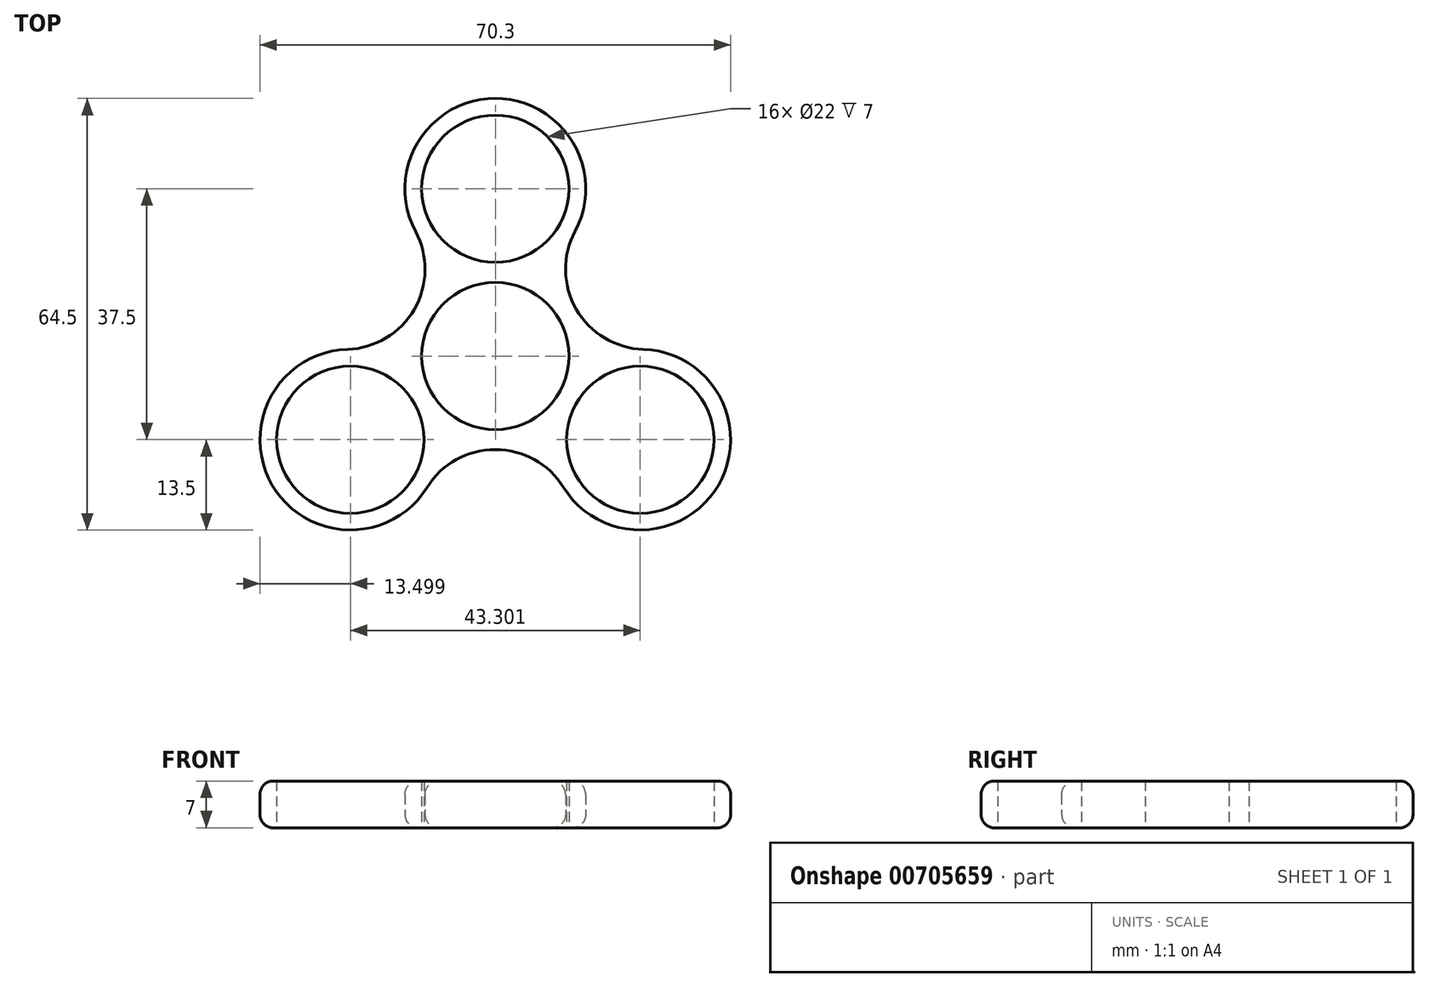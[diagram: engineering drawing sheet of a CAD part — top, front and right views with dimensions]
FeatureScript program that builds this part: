
annotation { "Feature Type Name" : "Feature", "Feature Type Description" : "" }
export const myFeature = defineFeature(function(context is Context, id is Id, definition is map)
    precondition{}
    {
        {
            var Q0;
            Q0=qCreatedBy(makeId("Top.planeOp"),FACE);
            var sketch = newSketch(context, id + "F0", { "sketchPlane" : qUnion([Q0])});
            skCircle(sketch, "E0.cCircle", {"center": v(0, 0) * mm, "radius": 12.5 * mm, "construction": true});
            skLineSegment(sketch, "E0.0", {"start": v(21.65, -12.5) * mm, "end": v(-21.65, -12.5) * mm, "construction": true});
            skLineSegment(sketch, "E0.1", {"start": v(-21.65, -12.5) * mm, "end": v(0, 25) * mm, "construction": true});
            skLineSegment(sketch, "E0.2", {"start": v(0, 25) * mm, "end": v(21.65, -12.5) * mm, "construction": true});
            skPoint(sketch, "E0.0.midPoint", {"position": v(0, -12.5) * mm});
            skCircle(sketch, "E1", {"center": v(0, 25) * mm, "radius": 13.5 * mm});
            skCircle(sketch, "E2.1.0", {"center": v(-21.65, -12.5) * mm, "radius": 13.5 * mm});
            skCircle(sketch, "E2.2.0", {"center": v(21.65, -12.5) * mm, "radius": 13.5 * mm});
            skArc(sketch, "E3", {"start": v(-22.1, 1) * mm, "mid": v(-12.1, 6.99) * mm, "end": v(-11.9, 18.64) * mm});
            skArc(sketch, "E4.1.0", {"start": v(10.19, -19.63) * mm, "mid": v(0, -13.97) * mm, "end": v(-10.19, -19.63) * mm});
            skArc(sketch, "E4.2.0", {"start": v(11.9, 18.64) * mm, "mid": v(12.1, 6.99) * mm, "end": v(22.1, 1) * mm});
            skCircle(sketch, "E5", {"center": v(0, 25) * mm, "radius": 11 * mm});
            skCircle(sketch, "E6.1.0", {"center": v(-21.65, -12.5) * mm, "radius": 11 * mm});
            skCircle(sketch, "E6.2.0", {"center": v(21.65, -12.5) * mm, "radius": 11 * mm});
            skCircle(sketch, "E7", {"center": v(0, 0) * mm, "radius": 11 * mm});
            skSolve(sketch);
        }
        {
            var Q0;
            Q0 = qSketchRegion(id + "F0", true);
            extrude(context, id + "F1", {"entities" : qUnion([Q0]), "depth" : 7 * mm, "offsetDistance" : 25 * mm});
        }
        {
            var Q0;
            Q0=makeQuery(id+"F1.opExtrude","CAP_EDGE",EDGE,{"disambiguationData":[OSD([sQuery(id+"F0.wireOp",EDGE,"E2.1.0")])],"isStart":false});
            var Q1;
            Q1=makeQuery(id+"F1.opExtrude","CAP_EDGE",EDGE,{"disambiguationData":[OSD([sQuery(id+"F0.wireOp",EDGE,"E2.1.0")])],"isStart":true});
            fillet(context, id + "F2", {"entities" : qUnion([Q0, Q1]), "radius" : 2 * mm, "tangentPropagation" : true, "allowEdgeOverflow" : false});
        }
    });
